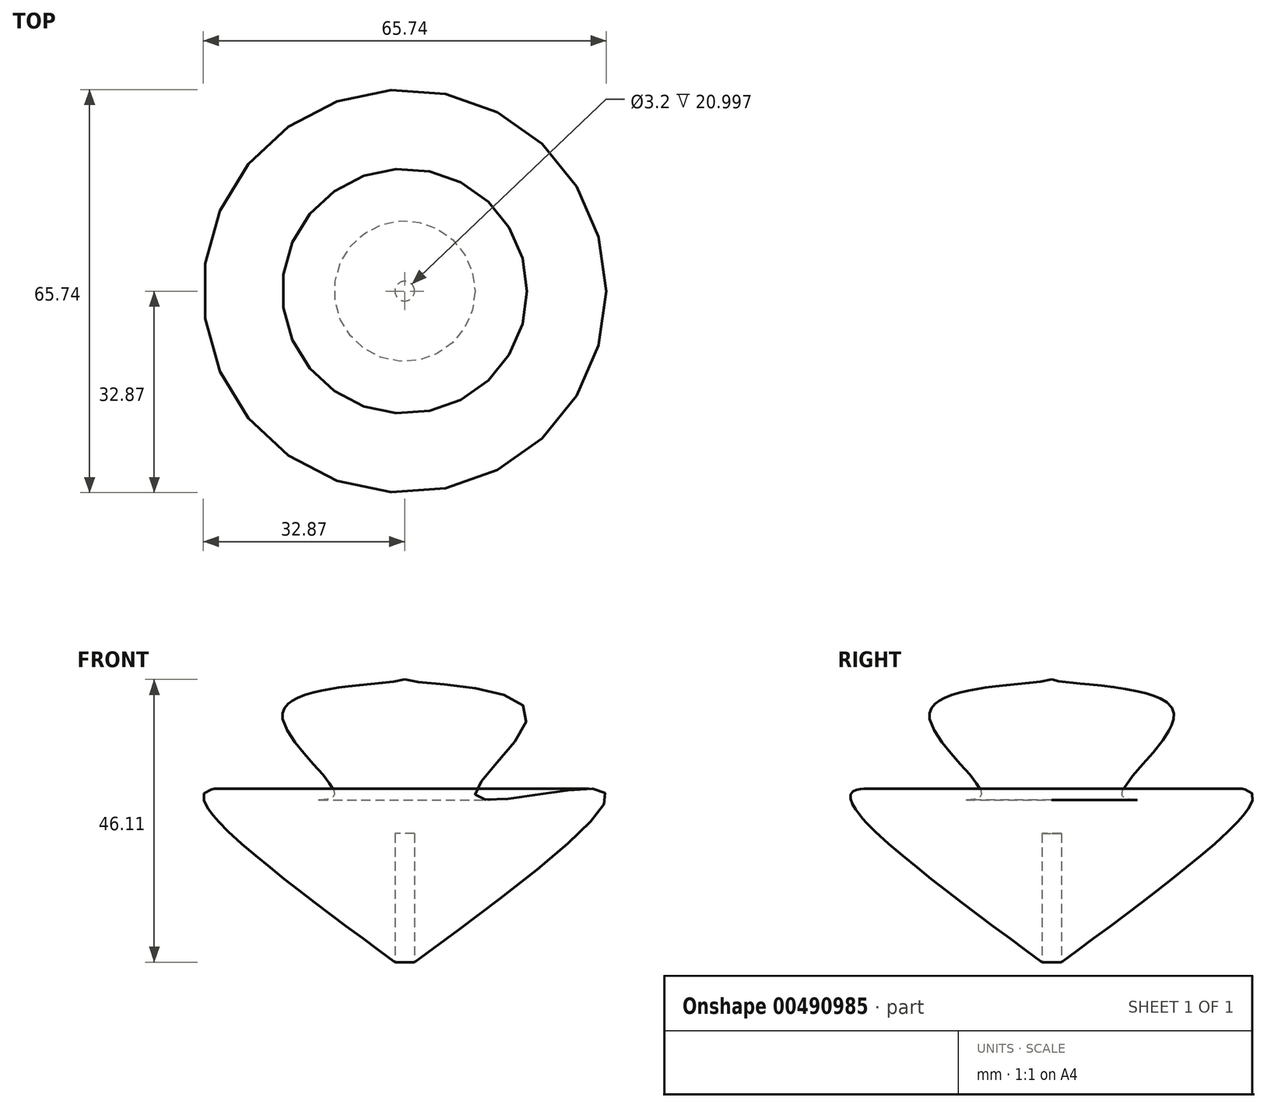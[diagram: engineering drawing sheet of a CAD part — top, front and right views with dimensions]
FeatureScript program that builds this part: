
annotation { "Feature Type Name" : "Feature", "Feature Type Description" : "" }
export const myFeature = defineFeature(function(context is Context, id is Id, definition is map)
    precondition{}
    {
        {
            var Q0;
            Q0=qCreatedBy(makeId("Front.planeOp"),FACE);
            var sketch = newSketch(context, id + "F0", { "sketchPlane" : qUnion([Q0])});
            skFitSpline(sketch, "E0", {"points": [v(0, 0) * mm, v(31.83, 29.3) * mm, v(11.53, 28.37) * mm, v(19.84, 42.22) * mm, v(0, 47.3) * mm, v(0, 47.75) * mm], "startDerivative": vector(173.85, 127.83) * mm, "endDerivative": vector(10.26, 14.6) * mm});
            skLineSegment(sketch, "E1", {"start": v(0, 47.75) * mm, "end": v(0, 0) * mm});
            skSolve(sketch);
        }
        {
            var Q0;
            {var subQ0=sQuery(id+"F0.wireOp",EDGE,"E1");var subQ1=sQuery(id+"F0.wireOp",EDGE,"E0");var subQ2=makeQuery(id+"F0.imprint","INTERSECT",VERTEX,{"disambiguationData":[OD(0.0)],"derivedFrom":[subQ1,subQ0]});Q0=makeQuery(id+"F0.imprint","IMPRINT",FACE,{"disambiguationData":[TD([[makeQuery(id+"F0.imprint","IMPRINT",EDGE,{"disambiguationData":[TD([[subQ2,-1.0]])],"derivedFrom":subQ1}),1.0]])]});}
            var Q1;
            Q1=sQuery(id+"F0.wireOp",EDGE,"E1");
            revolve(context, id + "F1", {"entities" : qUnion([Q0]), "axis" : qUnion([Q1]), "revolveType" : RevolveType.FULL});
        }
        {
            var Q0;
            Q0=qCreatedBy(makeId("Top.planeOp"),FACE);
            var sketch = newSketch(context, id + "F2", { "sketchPlane" : qUnion([Q0])});
            skCircle(sketch, "E2", {"center": v(0, 0) * mm, "radius": 1.6 * mm});
            skSolve(sketch);
        }
        {
            var Q0;
            Q0=makeQuery(id+"F2.imprint","IMPRINT",FACE,{"disambiguationData":[TD([[makeQuery(id+"F2.imprint","IMPRINT",EDGE,{"derivedFrom":sQuery(id+"F2.wireOp",EDGE,"E2")}),1.0]])]});
            var Q1;
            Q1=sQuery(id+"F2.wireOp",EDGE,"E2");
            extrude(context, id + "F3", {"entities" : qUnion([Q0]), "operationType" : NewBodyOperationType.REMOVE, "surfaceEntities" : qUnion([Q1]), "depth" : 22.17 * mm});
        }
    });
